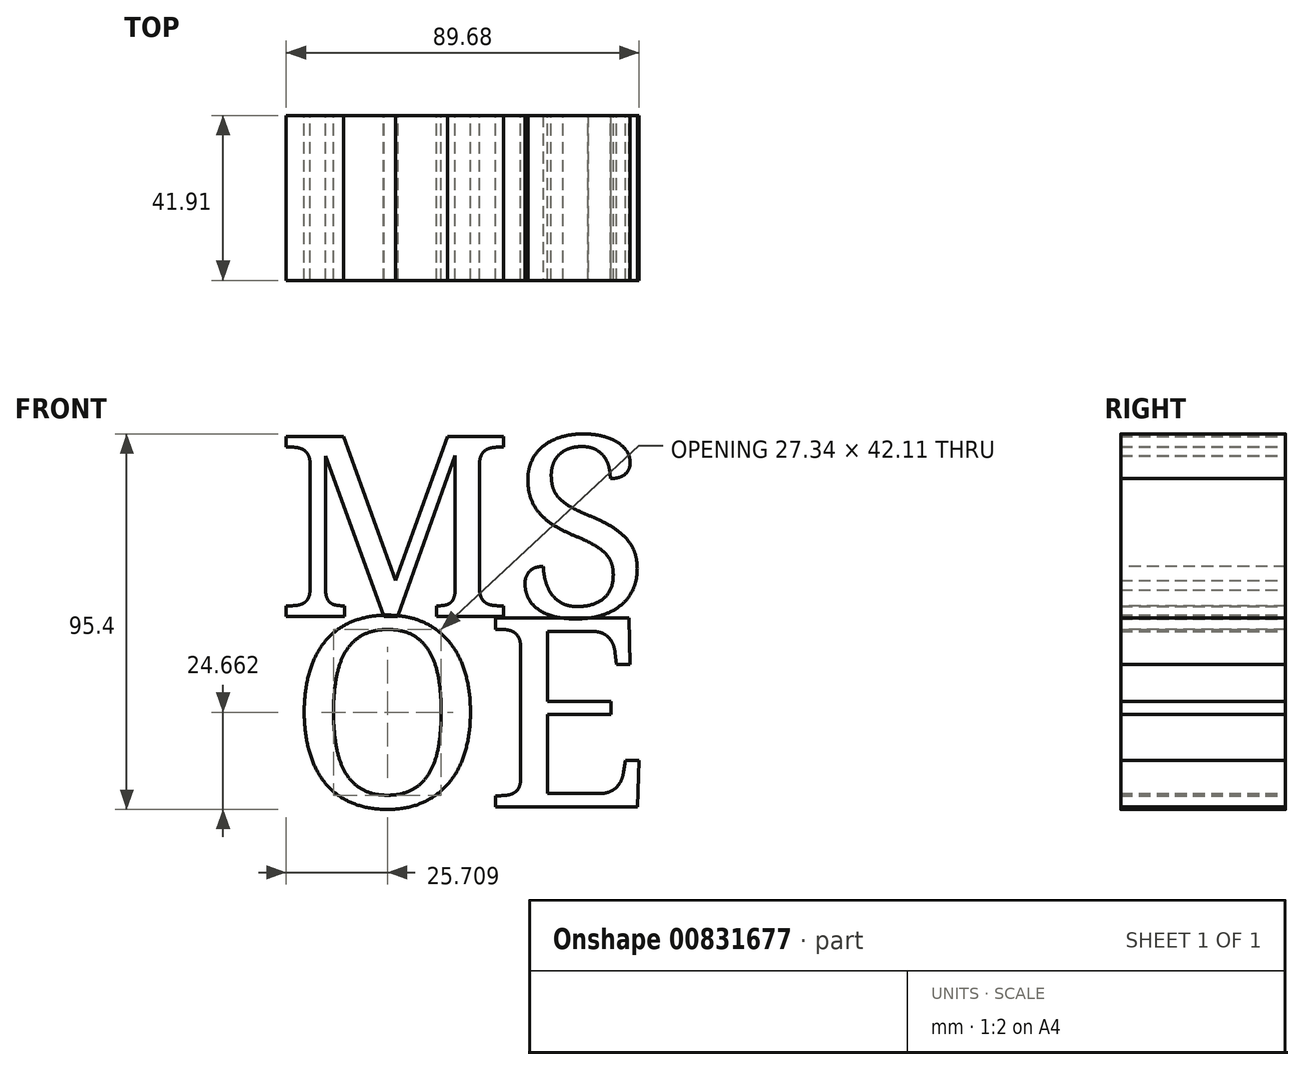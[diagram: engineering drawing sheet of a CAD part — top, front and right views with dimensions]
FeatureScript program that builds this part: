
annotation { "Feature Type Name" : "Feature", "Feature Type Description" : "" }
export const myFeature = defineFeature(function(context is Context, id is Id, definition is map)
    precondition{}
    {
        {
            var Q0;
            Q0=qCreatedBy(makeId("Front.planeOp"),FACE);
            var sketch = newSketch(context, id + "F0", { "sketchPlane" : qUnion([Q0])});
            skLineSegment(sketch, "E0.bottom", {"start": v(-50.8, -50.8) * mm, "end": v(50.8, -50.8) * mm});
            skLineSegment(sketch, "E0.top", {"start": v(-50.8, 50.8) * mm, "end": v(50.8, 50.8) * mm});
            skLineSegment(sketch, "E0.left", {"start": v(-50.8, -50.8) * mm, "end": v(-50.8, 50.8) * mm});
            skLineSegment(sketch, "E0.right", {"start": v(50.8, -50.8) * mm, "end": v(50.8, 50.8) * mm});
            skPoint(sketch, "E0.middle", {"position": v(0, 0) * mm});
            skText(sketch, "E1", { "text": "MS", "fontName": "NotoSerif-Regular.ttf"});
            skText(sketch, "E2", { "text": "OE", "fontName": "NotoSerif-Regular.ttf"});
            const initialGuessF0  = {"E1": [-0.05089, 0.00102, 1, 0, 0.0461], "E2": [-0.04763, -0.04736, 1, 0, 0.04835]};
            skSetInitialGuess(sketch, initialGuessF0);
            skSolve(sketch);
        }
        {
            var Q0;
            {var subQ0=sQuery(id+"F0.wireOp",EDGE,"E1.sketch_text.stroke-50");Q0=makeQuery(id+"F0.imprint","IMPRINT",FACE,{"disambiguationData":[TD([[makeQuery(id+"F0.imprint","IMPRINT",EDGE,{"derivedFrom":subQ0}),-1.0]])]});}
            var Q1;
            Q1=makeQuery(id+"F0.imprint","IMPRINT",FACE,{"disambiguationData":[TD([[makeQuery(id+"F0.imprint","IMPRINT",EDGE,{"derivedFrom":sQuery(id+"F0.wireOp",EDGE,"E2.sketch_text.stroke-32")}),-1.0]])]});
            var Q2;
            {var subQ8=sQuery(id+"F0.wireOp",EDGE,"E1.sketch_text.stroke-8");Q2=makeQuery(id+"F0.imprint","IMPRINT",FACE,{"disambiguationData":[TD([[makeQuery(id+"F0.imprint","IMPRINT",EDGE,{"derivedFrom":subQ8}),1.0]])]});}
            var Q3;
            Q3=makeQuery(id+"F0.imprint","IMPRINT",FACE,{"disambiguationData":[TD([[makeQuery(id+"F0.imprint","IMPRINT",EDGE,{"derivedFrom":sQuery(id+"F0.wireOp",EDGE,"E1.sketch_text.stroke-0")}),-1.0]])]});
            var Q4;
            Q4=qCreatedBy(makeId("Front.planeOp"),FACE);
            extrude(context, id + "F1", {"entities" : qUnion([Q0, Q1, Q2, Q3]), "depth" : 41.9 * mm, "endBoundEntityFace" : qUnion([Q4]), "offsetDistance" : 25.4 * mm});
        }
    });
